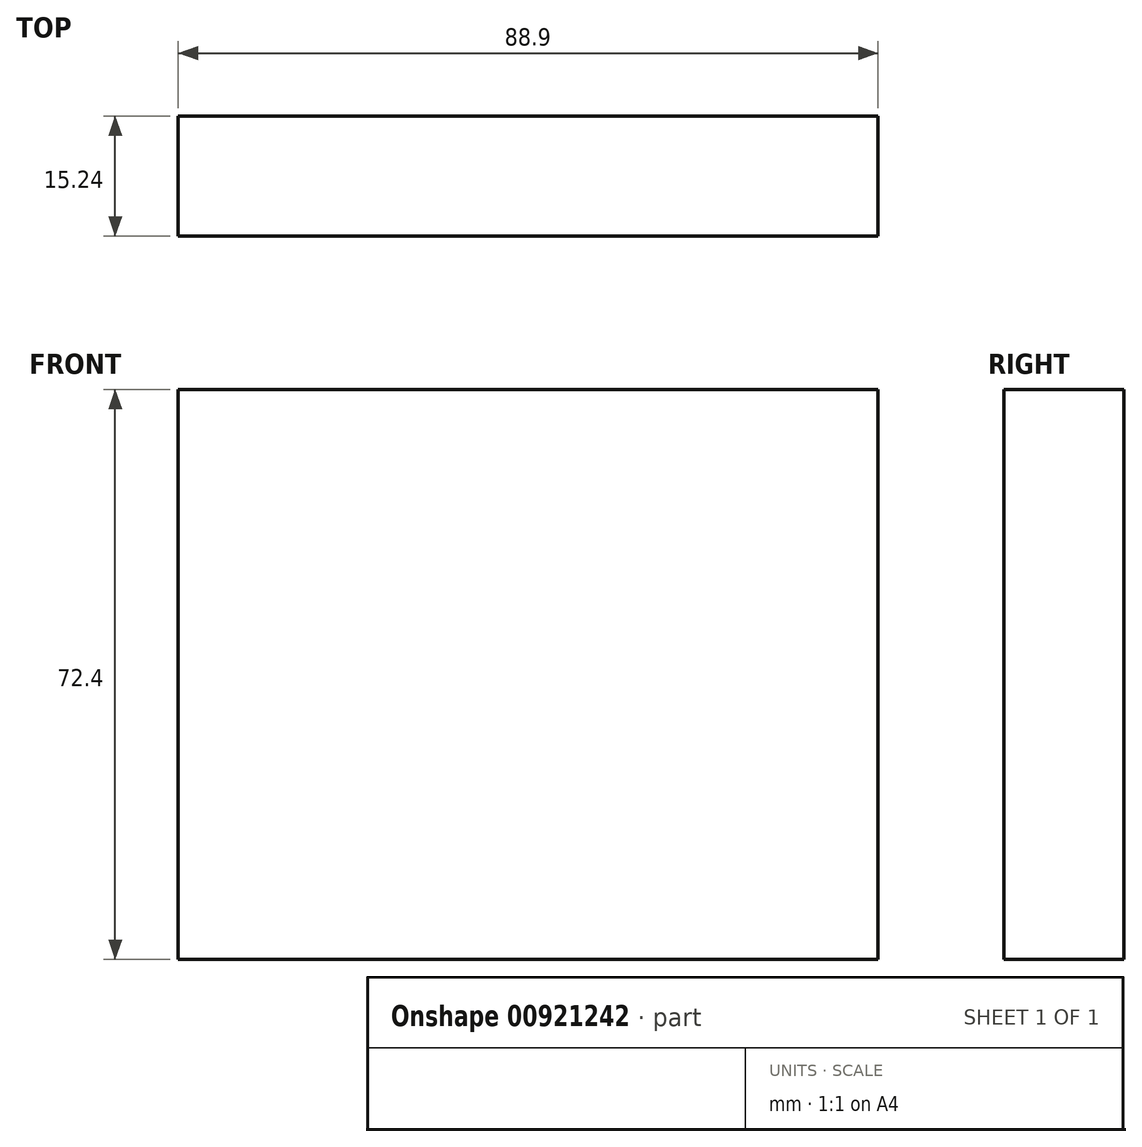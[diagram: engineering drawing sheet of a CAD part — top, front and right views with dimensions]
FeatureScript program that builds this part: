
annotation { "Feature Type Name" : "Feature", "Feature Type Description" : "" }
export const myFeature = defineFeature(function(context is Context, id is Id, definition is map)
    precondition{}
    {
        {
            var Q0;
            Q0=qCreatedBy(makeId("Front.planeOp"),FACE);
            var sketch = newSketch(context, id + "F0", { "sketchPlane" : qUnion([Q0])});
            skLineSegment(sketch, "E0.bottom", {"start": v(44.45, 36.2) * mm, "end": v(-44.45, 36.2) * mm});
            skLineSegment(sketch, "E0.top", {"start": v(44.45, -36.2) * mm, "end": v(-44.45, -36.2) * mm});
            skLineSegment(sketch, "E0.left", {"start": v(44.45, 36.2) * mm, "end": v(44.45, -36.2) * mm});
            skLineSegment(sketch, "E0.right", {"start": v(-44.45, 36.2) * mm, "end": v(-44.45, -36.2) * mm});
            skPoint(sketch, "E0.middle", {"position": v(0, 0) * mm});
            skSolve(sketch);
        }
        {
            var Q0;
            Q0 = qSketchRegion(id + "F0", true);
            extrude(context, id + "F1", {"entities" : qUnion([Q0]), "depth" : 15.24 * mm, "offsetDistance" : 25.4 * mm});
        }
    });
